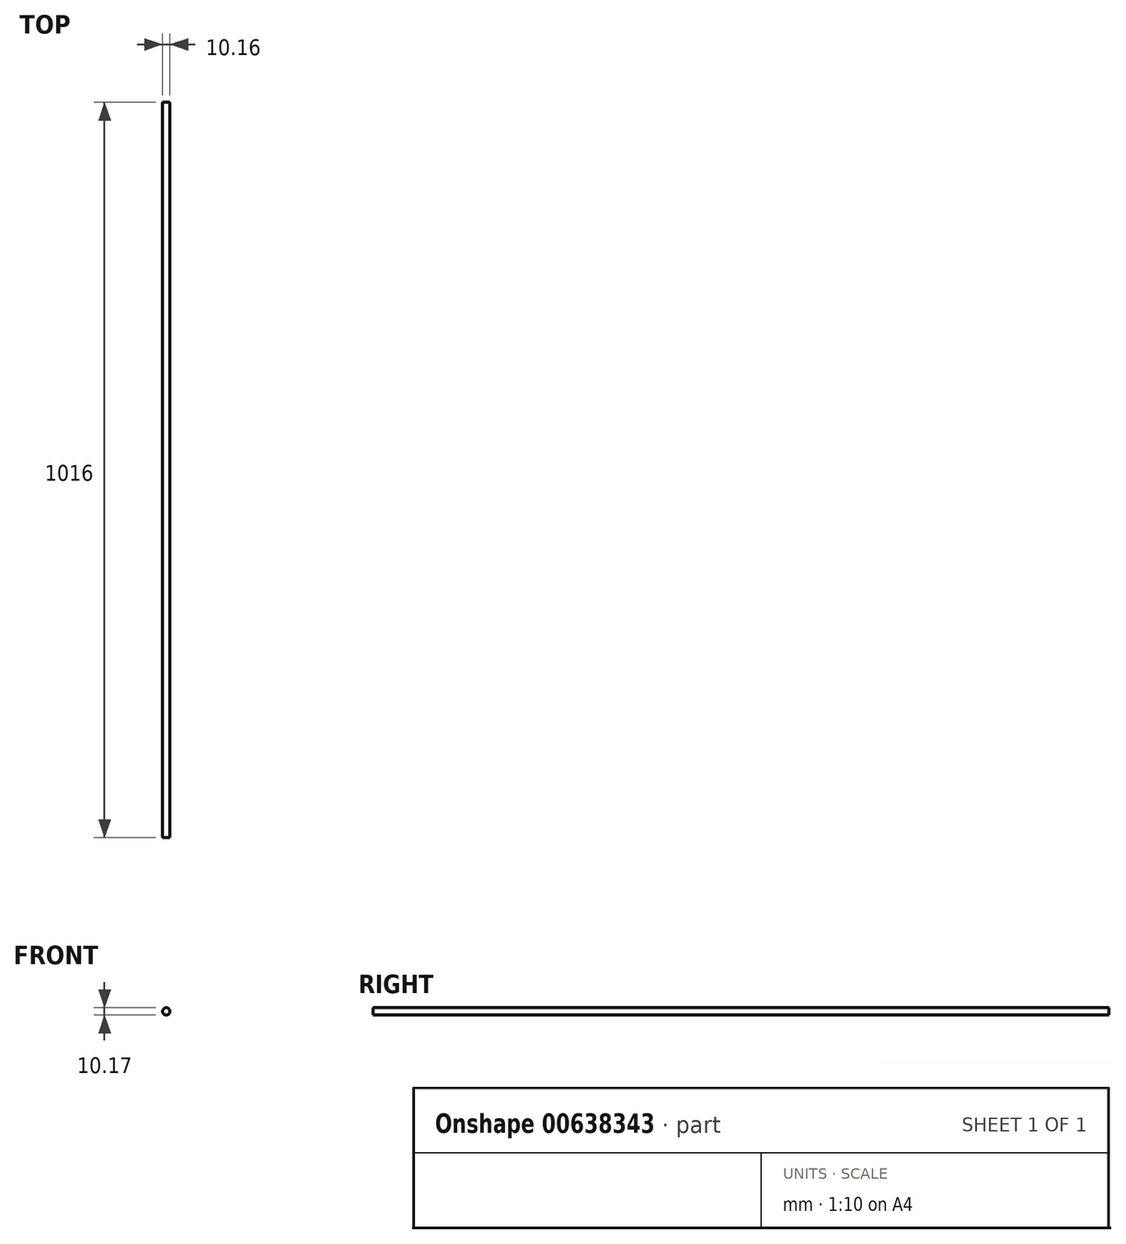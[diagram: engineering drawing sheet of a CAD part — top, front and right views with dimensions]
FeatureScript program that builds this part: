
annotation { "Feature Type Name" : "Feature", "Feature Type Description" : "" }
export const myFeature = defineFeature(function(context is Context, id is Id, definition is map)
    precondition{}
    {
        {
            var Q0;
            Q0=qCreatedBy(makeId("Front.planeOp"),FACE);
            var sketch = newSketch(context, id + "F0", { "sketchPlane" : qUnion([Q0])});
            skCircle(sketch, "E0", {"center": v(0, 24.2) * mm, "radius": 5.08 * mm});
            skSolve(sketch);
        }
        {
            var Q0;
            Q0 = qSketchRegion(id + "F0", true);
            extrude(context, id + "F1", {"entities" : qUnion([Q0]), "depth" : 1016 * mm, "offsetDistance" : 25.4 * mm});
        }
    });
